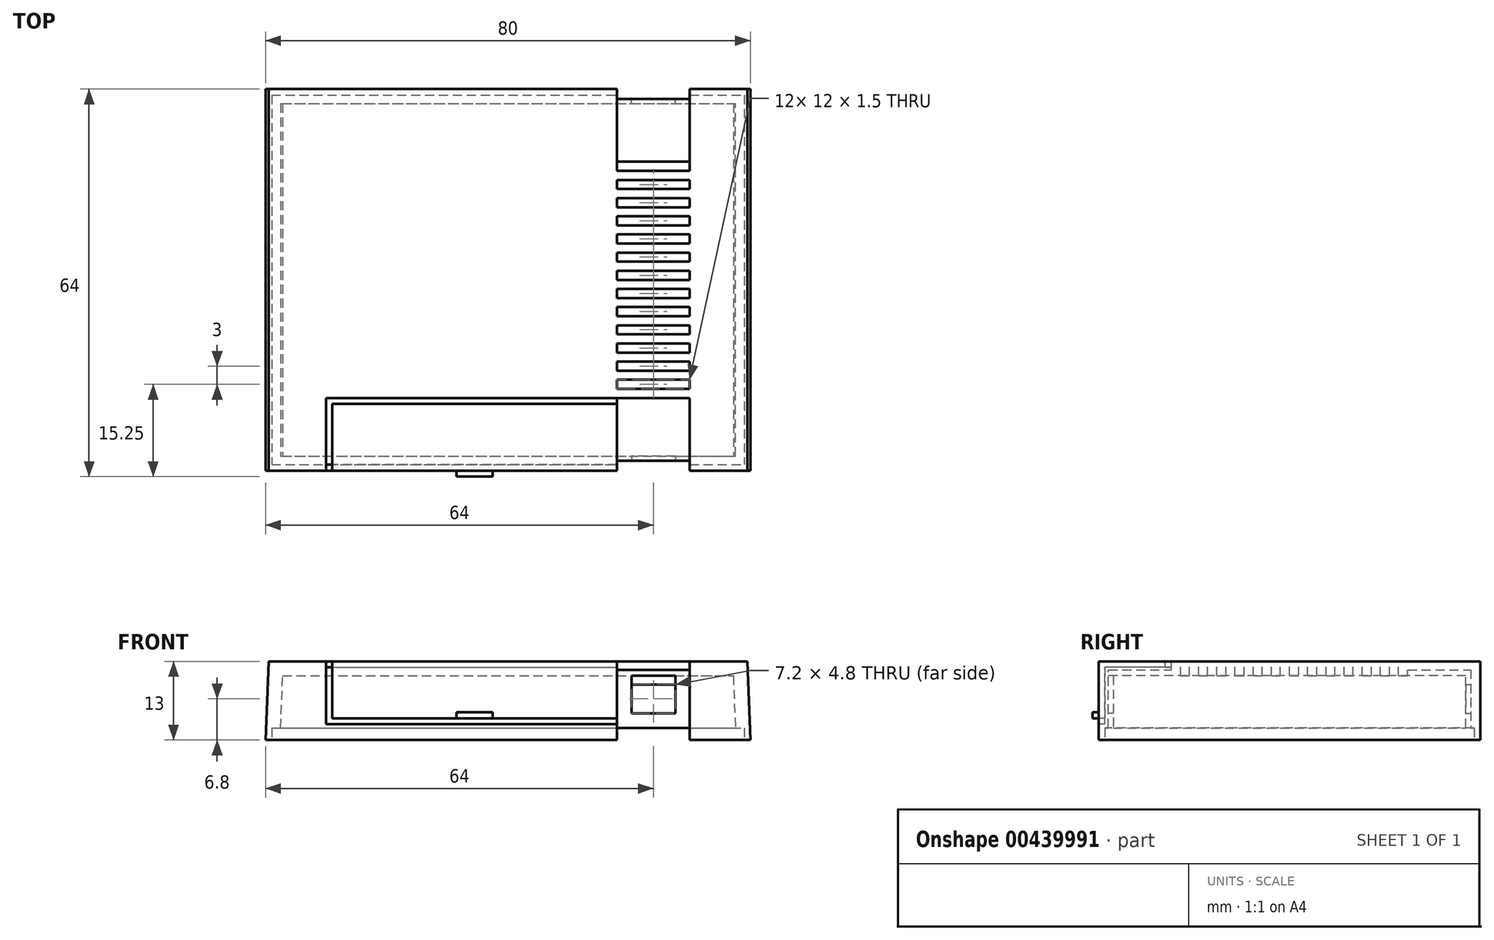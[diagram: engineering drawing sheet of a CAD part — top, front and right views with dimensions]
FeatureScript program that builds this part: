
annotation { "Feature Type Name" : "Feature", "Feature Type Description" : "" }
export const myFeature = defineFeature(function(context is Context, id is Id, definition is map)
    precondition{}
    {
        {
            var Q0;
            Q0=qCreatedBy(makeId("Top.planeOp"),FACE);
            var sketch = newSketch(context, id + "F0", { "sketchPlane" : qUnion([Q0])});
            skLineSegment(sketch, "E0.bottom", {"start": v(-40, 31.5) * mm, "end": v(40, 31.5) * mm});
            skLineSegment(sketch, "E0.top", {"start": v(-40, -31.5) * mm, "end": v(40, -31.5) * mm});
            skLineSegment(sketch, "E0.left", {"start": v(-40, 31.5) * mm, "end": v(-40, -31.5) * mm});
            skLineSegment(sketch, "E0.right", {"start": v(40, 31.5) * mm, "end": v(40, -31.5) * mm});
            skLineSegment(sketch, "E1.0", {"start": v(-39, -30.5) * mm, "end": v(39, -30.5) * mm});
            skLineSegment(sketch, "E1.1", {"start": v(-39, 30.5) * mm, "end": v(-39, -30.5) * mm});
            skLineSegment(sketch, "E1.2", {"start": v(-39, 30.5) * mm, "end": v(39, 30.5) * mm});
            skLineSegment(sketch, "E1.3", {"start": v(39, 30.5) * mm, "end": v(39, -30.5) * mm});
            skSolve(sketch);
        }
        {
            var Q0;
            Q0 = qSketchRegion(id + "F0", true);
            var Q1;
            Q1=makeQuery(id+"F0.imprint","IMPRINT",FACE,{"disambiguationData":[TD([[makeQuery(id+"F0.imprint","IMPRINT",EDGE,{"derivedFrom":sQuery(id+"F0.wireOp",EDGE,"E0.bottom")}),-1.0]])]});
            var Q2;
            Q2=makeQuery(id+"F0.imprint","IMPRINT",FACE,{"disambiguationData":[TD([[makeQuery(id+"F0.imprint","IMPRINT",EDGE,{"derivedFrom":sQuery(id+"F0.wireOp",EDGE,"E1.0")}),1.0]])]});
            extrude(context, id + "F1", {"entities" : qUnion([Q0, Q1, Q2]), "depth" : 13 * mm});
        }
        {
            var Q0;
            Q0=makeQuery(id+"F1.opExtrude","SWEPT_FACE",FACE,{"disambiguationData":[OSD([sQuery(id+"F0.wireOp",EDGE,"E0.top")])]});
            var sketch = newSketch(context, id + "F2", { "sketchPlane" : qUnion([Q0])});
            skLineSegment(sketch, "E2.0", {"start": v(-40, 13) * mm, "end": v(-40, 0) * mm});
            skLineSegment(sketch, "E2.1", {"start": v(-40, 13) * mm, "end": v(40, 13) * mm});
            skLineSegment(sketch, "E2.2", {"start": v(40, 13) * mm, "end": v(40, 0) * mm});
            skLineSegment(sketch, "E2.3", {"start": v(-40, 0) * mm, "end": v(40, 0) * mm});
            skPoint(sketch, "E3", {"position": v(-39.5, 13) * mm});
            skPoint(sketch, "E4", {"position": v(39.5, 13) * mm});
            skLineSegment(sketch, "E5", {"start": v(-40, 0) * mm, "end": v(-39.5, 13) * mm});
            skLineSegment(sketch, "E6", {"start": v(39.5, 13) * mm, "end": v(40, 0) * mm});
            skPoint(sketch, "E7", {"position": v(30, 0) * mm});
            skPoint(sketch, "E8", {"position": v(18, 0) * mm});
            skPoint(sketch, "E9", {"position": v(30, 13) * mm});
            skPoint(sketch, "E10", {"position": v(18, 13) * mm});
            skLineSegment(sketch, "E11", {"start": v(18, 0) * mm, "end": v(18, 13) * mm});
            skLineSegment(sketch, "E12", {"start": v(30, 0) * mm, "end": v(30, 13) * mm});
            skPoint(sketch, "E13", {"position": v(-30, 0) * mm});
            skLineSegment(sketch, "E14", {"start": v(-30, 0) * mm, "end": v(-30, 13) * mm});
            skPoint(sketch, "E15", {"position": v(-30, 2.6) * mm});
            skLineSegment(sketch, "E16", {"start": v(-30, 2.6) * mm, "end": v(18, 2.6) * mm});
            skLineSegment(sketch, "E17", {"start": v(-29, 13) * mm, "end": v(-29, 2.6) * mm});
            skLineSegment(sketch, "E18", {"start": v(18, 3.6) * mm, "end": v(-29, 3.6) * mm});
            skPoint(sketch, "E19", {"position": v(-5.5, 3.6) * mm});
            skPoint(sketch, "E20", {"position": v(-8.5, 3.6) * mm});
            skPoint(sketch, "E21", {"position": v(-2.5, 3.6) * mm});
            skPoint(sketch, "E22", {"position": v(-8.5, 4.6) * mm});
            skPoint(sketch, "E23", {"position": v(-2.5, 4.6) * mm});
            skLineSegment(sketch, "E24", {"start": v(-8.5, 3.6) * mm, "end": v(-8.5, 4.6) * mm});
            skLineSegment(sketch, "E25", {"start": v(-8.5, 4.6) * mm, "end": v(-2.5, 4.6) * mm});
            skLineSegment(sketch, "E26", {"start": v(-2.5, 4.6) * mm, "end": v(-2.5, 3.6) * mm});
            skSolve(sketch);
        }
        {
            var Q0;
            {var subQ0=sQuery(id+"F2.wireOp",EDGE,"E2.0");Q0=makeQuery(id+"F2.imprint","IMPRINT",FACE,{"disambiguationData":[TD([[makeQuery(id+"F2.imprint","IMPRINT",EDGE,{"derivedFrom":subQ0}),1.0]])]});}
            var Q1;
            {var subQ0=sQuery(id+"F2.wireOp",EDGE,"E2.2");Q1=makeQuery(id+"F2.imprint","IMPRINT",FACE,{"disambiguationData":[TD([[makeQuery(id+"F2.imprint","IMPRINT",EDGE,{"derivedFrom":subQ0}),-1.0]])]});}
            extrude(context, id + "F3", {"entities" : qUnion([Q0, Q1]), "operationType" : NewBodyOperationType.REMOVE, "oppositeDirection" : true, "depth" : 63 * mm});
        }
        {
            var Q0;
            Q0=makeQuery(id+"F1.opExtrude","CAP_FACE",FACE,{"disambiguationData":[OSD([sQuery(id+"F0.wireOp",EDGE,"E0.bottom"),sQuery(id+"F0.wireOp",EDGE,"E0.top"),sQuery(id+"F0.wireOp",EDGE,"E0.left"),sQuery(id+"F0.wireOp",EDGE,"E0.right")])],"isStart":true});
            shell(context, id + "F4", {"entities" : qUnion([Q0]), "thickness" : 2.4 * mm});
        }
        {
            var Q0;
            Q0=makeQuery(id+"F0.imprint","IMPRINT",FACE,{"disambiguationData":[TD([[makeQuery(id+"F0.imprint","IMPRINT",EDGE,{"derivedFrom":sQuery(id+"F0.wireOp",EDGE,"E1.0")}),1.0]])]});
            extrude(context, id + "F5", {"entities" : qUnion([Q0]), "operationType" : NewBodyOperationType.REMOVE, "depth" : 2 * mm});
        }
        {
            var Q0;
            {var subQ0=sQuery(id+"F2.wireOp",EDGE,"E11");Q0=makeQuery(id+"F2.imprint","IMPRINT",FACE,{"disambiguationData":[TD([[makeQuery(id+"F2.imprint","IMPRINT",EDGE,{"derivedFrom":subQ0}),-1.0]])]});}
            extrude(context, id + "F6", {"entities" : qUnion([Q0]), "operationType" : NewBodyOperationType.REMOVE, "oppositeDirection" : true, "depth" : 1.6 * mm});
        }
        {
            var Q0;
            Q0=makeQuery(id+"F6.boolean.opBoolean","COPY",FACE,{"derivedFrom":makeQuery(id+"F6.opExtrude","CAP_FACE",FACE,{"disambiguationData":[OSD([sQuery(id+"F2.wireOp",EDGE,"E2.1"),sQuery(id+"F2.wireOp",EDGE,"E2.3"),sQuery(id+"F2.wireOp",EDGE,"E11"),sQuery(id+"F2.wireOp",EDGE,"E12")])],"isStart":false})});
            var sketch = newSketch(context, id + "F7", { "sketchPlane" : qUnion([Q0])});
            skLineSegment(sketch, "E27.0", {"start": v(20.4, 4.4) * mm, "end": v(20.4, 10.6) * mm});
            skLineSegment(sketch, "E27.1", {"start": v(20.4, 4.4) * mm, "end": v(27.6, 4.4) * mm});
            skLineSegment(sketch, "E27.2", {"start": v(27.6, 4.4) * mm, "end": v(27.6, 10.6) * mm});
            skLineSegment(sketch, "E27.3", {"start": v(20.4, 10.6) * mm, "end": v(27.6, 10.6) * mm});
            skSolve(sketch);
        }
        {
            var Q0;
            Q0=makeQuery(id+"F7.imprint","IMPRINT",FACE,{"disambiguationData":[TD([[makeQuery(id+"F7.imprint","IMPRINT",EDGE,{"derivedFrom":sQuery(id+"F7.wireOp",EDGE,"E27.0")}),-1.0]])]});
            extrude(context, id + "F8", {"entities" : qUnion([Q0]), "operationType" : NewBodyOperationType.REMOVE, "oppositeDirection" : true, "depth" : 2 * mm});
        }
        {
            var Q0;
            Q0=makeQuery(id+"F1.opExtrude","CAP_FACE",FACE,{"disambiguationData":[OSD([sQuery(id+"F0.wireOp",EDGE,"E0.bottom"),sQuery(id+"F0.wireOp",EDGE,"E0.top"),sQuery(id+"F0.wireOp",EDGE,"E0.left"),sQuery(id+"F0.wireOp",EDGE,"E0.right")])],"isStart":false});
            var sketch = newSketch(context, id + "F9", { "sketchPlane" : qUnion([Q0])});
            skLineSegment(sketch, "E28.0", {"start": v(18, -29.9) * mm, "end": v(30, -29.9) * mm});
            skLineSegment(sketch, "E29", {"start": v(18, -29.9) * mm, "end": v(18, 31.5) * mm});
            skLineSegment(sketch, "E30", {"start": v(30, -29.9) * mm, "end": v(30, 31.5) * mm});
            skLineSegment(sketch, "E31.0", {"start": v(-40, -31.5) * mm, "end": v(40, -31.5) * mm});
            skLineSegment(sketch, "E32", {"start": v(18, -19.5) * mm, "end": v(30, -19.5) * mm});
            skLineSegment(sketch, "E33", {"start": v(18, 19.5) * mm, "end": v(30, 19.5) * mm});
            skLineSegment(sketch, "E34", {"start": v(18, 18) * mm, "end": v(30, 18) * mm});
            skLineSegment(sketch, "E35.0.1.0", {"start": v(18, 15) * mm, "end": v(30, 15) * mm});
            skLineSegment(sketch, "E35.0.1.1", {"start": v(18, 16.5) * mm, "end": v(30, 16.5) * mm});
            skLineSegment(sketch, "E35.0.2.0", {"start": v(18, 12) * mm, "end": v(30, 12) * mm});
            skLineSegment(sketch, "E35.0.2.1", {"start": v(18, 13.5) * mm, "end": v(30, 13.5) * mm});
            skLineSegment(sketch, "E35.0.3.0", {"start": v(18, 9) * mm, "end": v(30, 9) * mm});
            skLineSegment(sketch, "E35.0.3.1", {"start": v(18, 10.5) * mm, "end": v(30, 10.5) * mm});
            skLineSegment(sketch, "E35.0.4.0", {"start": v(18, 6) * mm, "end": v(30, 6) * mm});
            skLineSegment(sketch, "E35.0.4.1", {"start": v(18, 7.5) * mm, "end": v(30, 7.5) * mm});
            skLineSegment(sketch, "E35.0.5.0", {"start": v(18, 3) * mm, "end": v(30, 3) * mm});
            skLineSegment(sketch, "E35.0.5.1", {"start": v(18, 4.5) * mm, "end": v(30, 4.5) * mm});
            skLineSegment(sketch, "E35.0.6.0", {"start": v(18, 0) * mm, "end": v(30, 0) * mm});
            skLineSegment(sketch, "E35.0.6.1", {"start": v(18, 1.5) * mm, "end": v(30, 1.5) * mm});
            skLineSegment(sketch, "E35.0.7.0", {"start": v(18, -3) * mm, "end": v(30, -3) * mm});
            skLineSegment(sketch, "E35.0.7.1", {"start": v(18, -1.5) * mm, "end": v(30, -1.5) * mm});
            skLineSegment(sketch, "E35.0.8.0", {"start": v(18, -6) * mm, "end": v(30, -6) * mm});
            skLineSegment(sketch, "E35.0.8.1", {"start": v(18, -4.5) * mm, "end": v(30, -4.5) * mm});
            skLineSegment(sketch, "E35.0.9.0", {"start": v(18, -9) * mm, "end": v(30, -9) * mm});
            skLineSegment(sketch, "E35.0.9.1", {"start": v(18, -7.5) * mm, "end": v(30, -7.5) * mm});
            skLineSegment(sketch, "E35.0.10.0", {"start": v(18, -12) * mm, "end": v(30, -12) * mm});
            skLineSegment(sketch, "E35.0.10.1", {"start": v(18, -10.5) * mm, "end": v(30, -10.5) * mm});
            skLineSegment(sketch, "E35.0.11.0", {"start": v(18, -15) * mm, "end": v(30, -15) * mm});
            skLineSegment(sketch, "E35.0.11.1", {"start": v(18, -13.5) * mm, "end": v(30, -13.5) * mm});
            skLineSegment(sketch, "E35.0.12.0", {"start": v(18, -18) * mm, "end": v(30, -18) * mm});
            skLineSegment(sketch, "E35.0.12.1", {"start": v(18, -16.5) * mm, "end": v(30, -16.5) * mm});
            skLineSegment(sketch, "E35.direction1", {"start": v(18, 18) * mm, "end": v(39.8, 18) * mm, "construction": true});
            skLineSegment(sketch, "E35.direction2", {"start": v(18, 18) * mm, "end": v(18, 15) * mm, "construction": true});
            skPoint(sketch, "E36.0", {"position": v(-30, -31.5) * mm});
            skPoint(sketch, "E37", {"position": v(-30, -19.5) * mm});
            skLineSegment(sketch, "E38", {"start": v(-30, -19.5) * mm, "end": v(18, -19.5) * mm});
            skLineSegment(sketch, "E39", {"start": v(-30, -19.5) * mm, "end": v(-30, -31.5) * mm});
            skPoint(sketch, "E40", {"position": v(18, -20.5) * mm});
            skPoint(sketch, "E41", {"position": v(-29, -31.5) * mm});
            skPoint(sketch, "E42", {"position": v(-29, -20.5) * mm});
            skLineSegment(sketch, "E43", {"start": v(-29, -20.5) * mm, "end": v(-29, -31.5) * mm});
            skLineSegment(sketch, "E44", {"start": v(-29, -20.5) * mm, "end": v(18, -20.5) * mm});
            skSolve(sketch);
        }
        {
            var Q0;
            {var subQ3=sQuery(id+"F9.wireOp",EDGE,"E33");Q0=makeQuery(id+"F9.imprint","IMPRINT",FACE,{"disambiguationData":[TD([[makeQuery(id+"F9.imprint","IMPRINT",EDGE,{"derivedFrom":subQ3}),1.0]])]});}
            var Q1;
            {var subQ0=sQuery(id+"F9.wireOp",EDGE,"E28.0");Q1=makeQuery(id+"F9.imprint","IMPRINT",FACE,{"disambiguationData":[TD([[makeQuery(id+"F9.imprint","IMPRINT",EDGE,{"derivedFrom":subQ0}),1.0]])]});}
            extrude(context, id + "F10", {"entities" : qUnion([Q0, Q1]), "operationType" : NewBodyOperationType.REMOVE, "oppositeDirection" : true, "depth" : 1.4 * mm});
        }
        {
            var Q0;
            {var subQ0=sQuery(id+"F9.wireOp",EDGE,"E35.0.12.0");Q0=makeQuery(id+"F9.imprint","IMPRINT",FACE,{"disambiguationData":[TD([[makeQuery(id+"F9.imprint","IMPRINT",EDGE,{"derivedFrom":subQ0}),1.0]])]});}
            var Q1;
            {var subQ0=sQuery(id+"F9.wireOp",EDGE,"E35.0.11.0");Q1=makeQuery(id+"F9.imprint","IMPRINT",FACE,{"disambiguationData":[TD([[makeQuery(id+"F9.imprint","IMPRINT",EDGE,{"derivedFrom":subQ0}),1.0]])]});}
            var Q2;
            {var subQ0=sQuery(id+"F9.wireOp",EDGE,"E35.0.10.0");Q2=makeQuery(id+"F9.imprint","IMPRINT",FACE,{"disambiguationData":[TD([[makeQuery(id+"F9.imprint","IMPRINT",EDGE,{"derivedFrom":subQ0}),1.0]])]});}
            var Q3;
            {var subQ0=sQuery(id+"F9.wireOp",EDGE,"E35.0.9.0");Q3=makeQuery(id+"F9.imprint","IMPRINT",FACE,{"disambiguationData":[TD([[makeQuery(id+"F9.imprint","IMPRINT",EDGE,{"derivedFrom":subQ0}),1.0]])]});}
            var Q4;
            {var subQ0=sQuery(id+"F9.wireOp",EDGE,"E35.0.8.0");Q4=makeQuery(id+"F9.imprint","IMPRINT",FACE,{"disambiguationData":[TD([[makeQuery(id+"F9.imprint","IMPRINT",EDGE,{"derivedFrom":subQ0}),1.0]])]});}
            var Q5;
            {var subQ0=sQuery(id+"F9.wireOp",EDGE,"E35.0.6.0");Q5=makeQuery(id+"F9.imprint","IMPRINT",FACE,{"disambiguationData":[TD([[makeQuery(id+"F9.imprint","IMPRINT",EDGE,{"derivedFrom":subQ0}),1.0]])]});}
            var Q6;
            {var subQ0=sQuery(id+"F9.wireOp",EDGE,"E35.0.7.0");Q6=makeQuery(id+"F9.imprint","IMPRINT",FACE,{"disambiguationData":[TD([[makeQuery(id+"F9.imprint","IMPRINT",EDGE,{"derivedFrom":subQ0}),1.0]])]});}
            var Q7;
            {var subQ0=sQuery(id+"F9.wireOp",EDGE,"E35.0.5.0");Q7=makeQuery(id+"F9.imprint","IMPRINT",FACE,{"disambiguationData":[TD([[makeQuery(id+"F9.imprint","IMPRINT",EDGE,{"derivedFrom":subQ0}),1.0]])]});}
            var Q8;
            {var subQ0=sQuery(id+"F9.wireOp",EDGE,"E35.0.4.0");Q8=makeQuery(id+"F9.imprint","IMPRINT",FACE,{"disambiguationData":[TD([[makeQuery(id+"F9.imprint","IMPRINT",EDGE,{"derivedFrom":subQ0}),1.0]])]});}
            var Q9;
            {var subQ0=sQuery(id+"F9.wireOp",EDGE,"E35.0.3.0");Q9=makeQuery(id+"F9.imprint","IMPRINT",FACE,{"disambiguationData":[TD([[makeQuery(id+"F9.imprint","IMPRINT",EDGE,{"derivedFrom":subQ0}),1.0]])]});}
            var Q10;
            {var subQ0=sQuery(id+"F9.wireOp",EDGE,"E35.0.2.0");Q10=makeQuery(id+"F9.imprint","IMPRINT",FACE,{"disambiguationData":[TD([[makeQuery(id+"F9.imprint","IMPRINT",EDGE,{"derivedFrom":subQ0}),1.0]])]});}
            var Q11;
            {var subQ0=sQuery(id+"F9.wireOp",EDGE,"E35.0.1.0");Q11=makeQuery(id+"F9.imprint","IMPRINT",FACE,{"disambiguationData":[TD([[makeQuery(id+"F9.imprint","IMPRINT",EDGE,{"derivedFrom":subQ0}),1.0]])]});}
            var Q12;
            {var subQ0=sQuery(id+"F9.wireOp",EDGE,"E33");Q12=makeQuery(id+"F9.imprint","IMPRINT",FACE,{"disambiguationData":[TD([[makeQuery(id+"F9.imprint","IMPRINT",EDGE,{"derivedFrom":subQ0}),-1.0]])]});}
            extrude(context, id + "F11", {"entities" : qUnion([Q0, Q1, Q2, Q3, Q4, Q5, Q6, Q7, Q8, Q9, Q10, Q11, Q12]), "operationType" : NewBodyOperationType.REMOVE, "oppositeDirection" : true, "depth" : 3 * mm});
        }
        {
            var Q0;
            Q0=makeQuery(id+"F1.opExtrude","SWEPT_FACE",FACE,{"disambiguationData":[OSD([sQuery(id+"F0.wireOp",EDGE,"E0.bottom")])]});
            var sketch = newSketch(context, id + "F12", { "sketchPlane" : qUnion([Q0])});
            skLineSegment(sketch, "E45.0", {"start": v(-18, 11.6) * mm, "end": v(-30, 11.6) * mm});
            skLineSegment(sketch, "E45.1", {"start": v(39, 0) * mm, "end": v(-39, 0) * mm});
            skLineSegment(sketch, "E46", {"start": v(-30, 11.6) * mm, "end": v(-30, 0) * mm});
            skLineSegment(sketch, "E47", {"start": v(-18, 11.6) * mm, "end": v(-18, 0) * mm});
            skSolve(sketch);
        }
        {
            var Q0;
            Q0=makeQuery(id+"F12.imprint","IMPRINT",FACE,{"disambiguationData":[TD([[makeQuery(id+"F12.imprint","IMPRINT",EDGE,{"derivedFrom":sQuery(id+"F12.wireOp",EDGE,"E45.0")}),1.0]])]});
            extrude(context, id + "F13", {"entities" : qUnion([Q0]), "operationType" : NewBodyOperationType.REMOVE, "oppositeDirection" : true, "depth" : 1.6 * mm});
        }
        {
            var Q0;
            Q0=makeQuery(id+"F13.boolean.opBoolean","COPY",FACE,{"derivedFrom":makeQuery(id+"F13.opExtrude","CAP_FACE",FACE,{"disambiguationData":[OSD([sQuery(id+"F12.wireOp",EDGE,"E45.0"),sQuery(id+"F12.wireOp",EDGE,"E45.1"),sQuery(id+"F12.wireOp",EDGE,"E46"),sQuery(id+"F12.wireOp",EDGE,"E47")])],"isStart":false})});
            var sketch = newSketch(context, id + "F14", { "sketchPlane" : qUnion([Q0])});
            skLineSegment(sketch, "E48.0", {"start": v(-20.4, 9.2) * mm, "end": v(-27.6, 9.2) * mm});
            skLineSegment(sketch, "E48.1", {"start": v(-20.4, 9.2) * mm, "end": v(-20.4, 4.4) * mm});
            skLineSegment(sketch, "E48.2", {"start": v(-27.6, 4.4) * mm, "end": v(-20.4, 4.4) * mm});
            skLineSegment(sketch, "E48.3", {"start": v(-27.6, 9.2) * mm, "end": v(-27.6, 4.4) * mm});
            skSolve(sketch);
        }
        {
            var Q0;
            Q0=makeQuery(id+"F14.imprint","IMPRINT",FACE,{"disambiguationData":[TD([[makeQuery(id+"F14.imprint","IMPRINT",EDGE,{"derivedFrom":sQuery(id+"F14.wireOp",EDGE,"E48.0")}),1.0]])]});
            extrude(context, id + "F15", {"entities" : qUnion([Q0]), "operationType" : NewBodyOperationType.REMOVE, "oppositeDirection" : true, "depth" : 3 * mm});
        }
        {
            var Q0;
            {var subQ1=sQuery(id+"F9.wireOp",EDGE,"E38");Q0=makeQuery(id+"F9.imprint","IMPRINT",FACE,{"disambiguationData":[TD([[makeQuery(id+"F9.imprint","IMPRINT",EDGE,{"derivedFrom":subQ1}),-1.0]])]});}
            extrude(context, id + "F16", {"entities" : qUnion([Q0]), "operationType" : NewBodyOperationType.REMOVE, "oppositeDirection" : true, "depth" : 1 * mm});
        }
        {
            var Q0;
            {var subQ0=sQuery(id+"F2.wireOp",EDGE,"E24");Q0=makeQuery(id+"F2.imprint","IMPRINT",FACE,{"disambiguationData":[TD([[makeQuery(id+"F2.imprint","IMPRINT",EDGE,{"derivedFrom":subQ0}),-1.0]])]});}
            extrude(context, id + "F17", {"entities" : qUnion([Q0]), "operationType" : NewBodyOperationType.ADD, "depth" : 1 * mm});
        }
        {
            var Q0;
            {var subQ1=sQuery(id+"F2.wireOp",EDGE,"E14");var subQ5=sQuery(id+"F2.wireOp",EDGE,"E2.1");var subQ6=makeQuery(id+"F2.imprint","INTERSECT",VERTEX,{"derivedFrom":[subQ5,subQ1]});Q0=makeQuery(id+"F2.imprint","IMPRINT",FACE,{"disambiguationData":[TD([[makeQuery(id+"F2.imprint","IMPRINT",EDGE,{"disambiguationData":[TD([[subQ6,-1.0]])],"derivedFrom":subQ5}),-1.0]])]});}
            var Q1;
            {var subQ1=sQuery(id+"F2.wireOp",EDGE,"E11");var subQ5=sQuery(id+"F2.wireOp",EDGE,"E16");var subQ8=makeQuery(id+"F2.imprint","INTERSECT",VERTEX,{"derivedFrom":[subQ1,subQ5]});Q1=makeQuery(id+"F2.imprint","IMPRINT",FACE,{"disambiguationData":[TD([[makeQuery(id+"F2.imprint","IMPRINT",EDGE,{"disambiguationData":[TD([[subQ8,-1.0]])],"derivedFrom":subQ1}),1.0]])]});}
            extrude(context, id + "F18", {"entities" : qUnion([Q0, Q1]), "operationType" : NewBodyOperationType.REMOVE, "oppositeDirection" : true, "depth" : 1 * mm});
        }
    });
